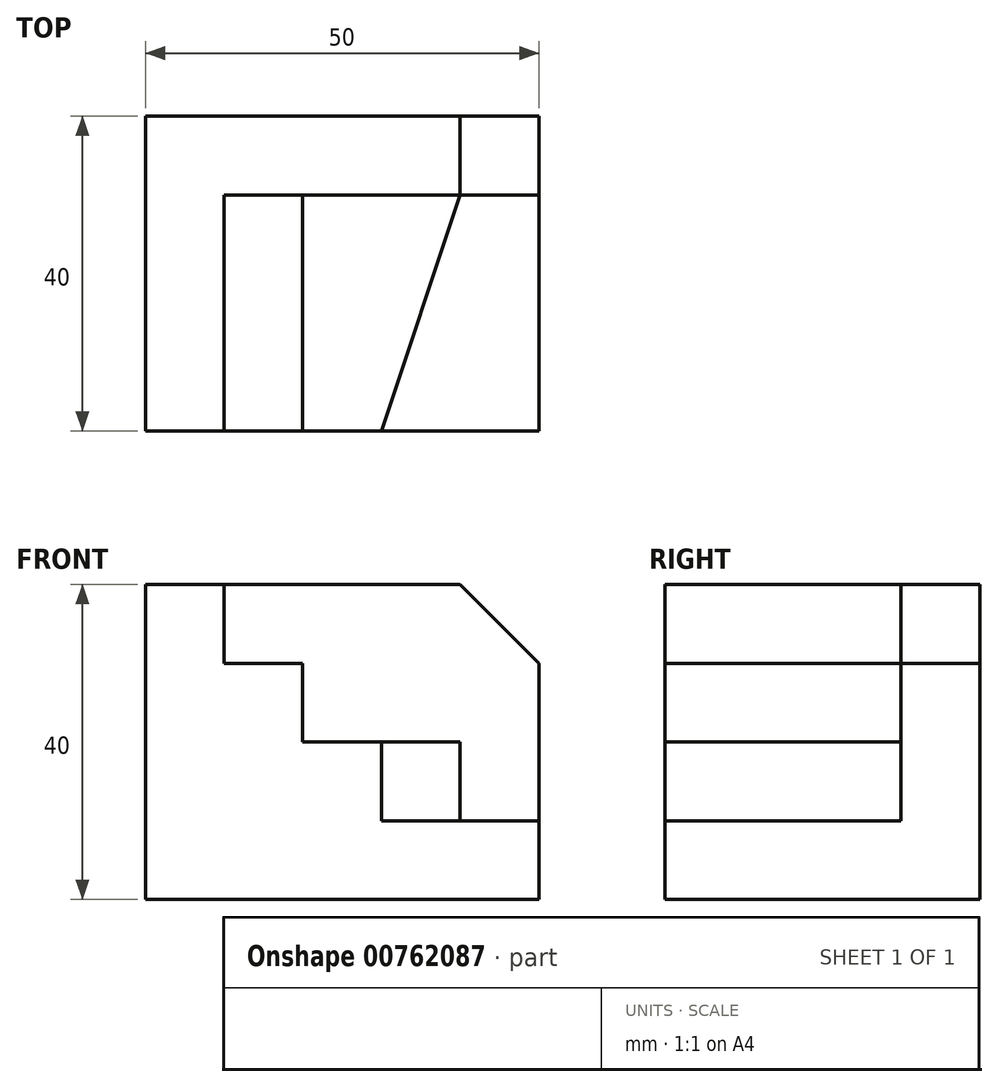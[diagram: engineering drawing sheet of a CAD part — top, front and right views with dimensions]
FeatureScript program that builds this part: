
annotation { "Feature Type Name" : "Feature", "Feature Type Description" : "" }
export const myFeature = defineFeature(function(context is Context, id is Id, definition is map)
    precondition{}
    {
        {
            var Q0;
            Q0=qCreatedBy(makeId("Top.planeOp"),FACE);
            var sketch = newSketch(context, id + "F0", { "sketchPlane" : qUnion([Q0])});
            skLineSegment(sketch, "E0.bottom", {"start": v(0, 0) * mm, "end": v(50, 0) * mm});
            skLineSegment(sketch, "E0.top", {"start": v(0, 40) * mm, "end": v(50, 40) * mm});
            skLineSegment(sketch, "E0.left", {"start": v(0, 0) * mm, "end": v(0, 40) * mm});
            skLineSegment(sketch, "E0.right", {"start": v(50, 0) * mm, "end": v(50, 40) * mm});
            skLineSegment(sketch, "E1", {"start": v(50, 30) * mm, "end": v(10, 30) * mm});
            skLineSegment(sketch, "E2", {"start": v(10, 30) * mm, "end": v(10, 0) * mm});
            skLineSegment(sketch, "E3", {"start": v(20, 30) * mm, "end": v(20, 0) * mm});
            skLineSegment(sketch, "E4", {"start": v(40, 30) * mm, "end": v(30, 0) * mm});
            skPoint(sketch, "E4.endSnap0", {"position": v(30, 30) * mm});
            skSolve(sketch);
        }
        {
            var Q0;
            {var subQ1=sQuery(id+"F0.wireOp",EDGE,"E0.top");Q0=makeQuery(id+"F0.imprint","IMPRINT",FACE,{"disambiguationData":[TD([[makeQuery(id+"F0.imprint","IMPRINT",EDGE,{"derivedFrom":subQ1}),-1.0]])]});}
            extrude(context, id + "F1", {"entities" : qUnion([Q0]), "flatOperationType" : FlatOperationType.REMOVE, "depth" : 40 * mm, "offsetDistance" : 25 * mm, "domain" : OperationDomain.MODEL});
        }
        {
            var Q0;
            {var subQ0=sQuery(id+"F0.wireOp",EDGE,"E2");Q0=makeQuery(id+"F0.imprint","IMPRINT",FACE,{"disambiguationData":[TD([[makeQuery(id+"F0.imprint","IMPRINT",EDGE,{"derivedFrom":subQ0}),1.0]])]});}
            extrude(context, id + "F2", {"entities" : qUnion([Q0]), "operationType" : NewBodyOperationType.ADD, "depth" : 30 * mm, "offsetDistance" : 25 * mm});
        }
        {
            var Q0;
            {var subQ0=sQuery(id+"F0.wireOp",EDGE,"E3");Q0=makeQuery(id+"F0.imprint","IMPRINT",FACE,{"disambiguationData":[TD([[makeQuery(id+"F0.imprint","IMPRINT",EDGE,{"derivedFrom":subQ0}),1.0]])]});}
            extrude(context, id + "F3", {"entities" : qUnion([Q0]), "operationType" : NewBodyOperationType.ADD, "depth" : 20 * mm, "offsetDistance" : 25 * mm});
        }
        {
            var Q0;
            {var subQ3=sQuery(id+"F0.wireOp",EDGE,"E4");Q0=makeQuery(id+"F0.imprint","IMPRINT",FACE,{"disambiguationData":[TD([[makeQuery(id+"F0.imprint","IMPRINT",EDGE,{"derivedFrom":subQ3}),1.0]])]});}
            extrude(context, id + "F4", {"entities" : qUnion([Q0]), "operationType" : NewBodyOperationType.ADD, "depth" : 10 * mm, "offsetDistance" : 25 * mm});
        }
        {
            var Q0;
            Q0=makeQuery(id+"F1.opExtrude","CAP_EDGE",EDGE,{"disambiguationData":[OSD([sQuery(id+"F0.wireOp",EDGE,"E0.right")])],"isStart":false});
            chamfer(context, id + "F5", {"entities" : qUnion([Q0]), "width" : 10 * mm, "tangentPropagation" : true});
        }
    });
